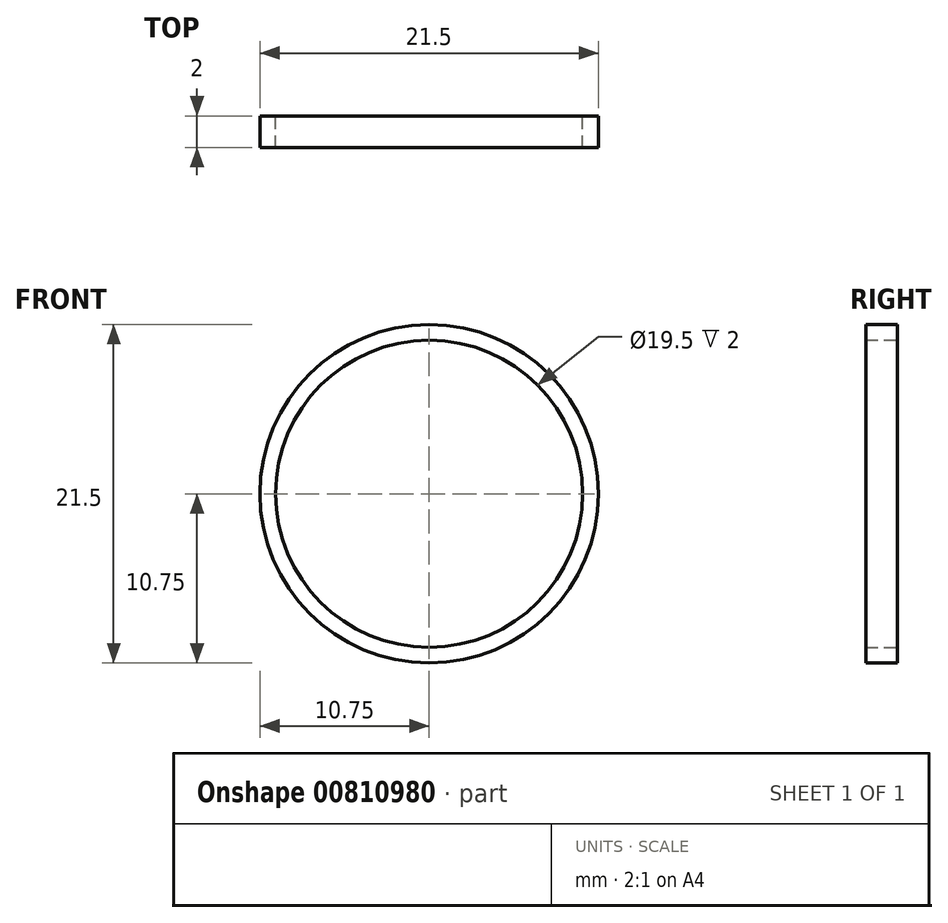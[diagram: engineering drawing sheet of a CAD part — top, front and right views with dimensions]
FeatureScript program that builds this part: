
annotation { "Feature Type Name" : "Feature", "Feature Type Description" : "" }
export const myFeature = defineFeature(function(context is Context, id is Id, definition is map)
    precondition{}
    {
        {
            var Q0;
            Q0=qCreatedBy(makeId("Front.planeOp"),FACE);
            var sketch = newSketch(context, id + "F0", { "sketchPlane" : qUnion([Q0])});
            skCircle(sketch, "E0", {"center": v(0, 0) * mm, "radius": 9.75 * mm});
            skCircle(sketch, "E1", {"center": v(0, 0) * mm, "radius": 10.75 * mm});
            skSolve(sketch);
        }
        {
            var Q0;
            Q0=makeQuery(id+"F0.imprint","IMPRINT",FACE,{"disambiguationData":[TD([[makeQuery(id+"F0.imprint","IMPRINT",EDGE,{"derivedFrom":sQuery(id+"F0.wireOp",EDGE,"E0")}),-1.0]])]});
            extrude(context, id + "F1", {"entities" : qUnion([Q0]), "depth" : 2 * mm, "offsetDistance" : 25 * mm});
        }
    });
